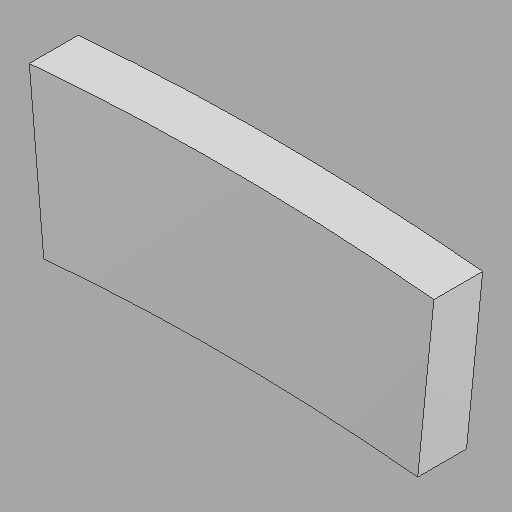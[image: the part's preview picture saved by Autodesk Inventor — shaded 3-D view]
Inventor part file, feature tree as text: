
AUTODESK INVENTOR PART (.ipt)
format: ipt  version: 2022.1 (Build 261234020, 234B)  size: 88,064 bytes
history: imported  units: in
note: dims shown in document units (in); Inventor stores cm internally (conversion verified against a paired STEP export)
features: imported_body x1
ambient origin geometry x8: Origin, YZ Plane, XZ Plane, XY Plane, X Axis, Y Axis, Z Axis, Center Point
bodies: Solid1 (imported_parasolid)
feature tree (1):
  imported_body  NMx_Import_Brep_tag  [imported B-rep: ~6 faces, bbox_mm=[1263.659676, 512.295091, 152.4]]
